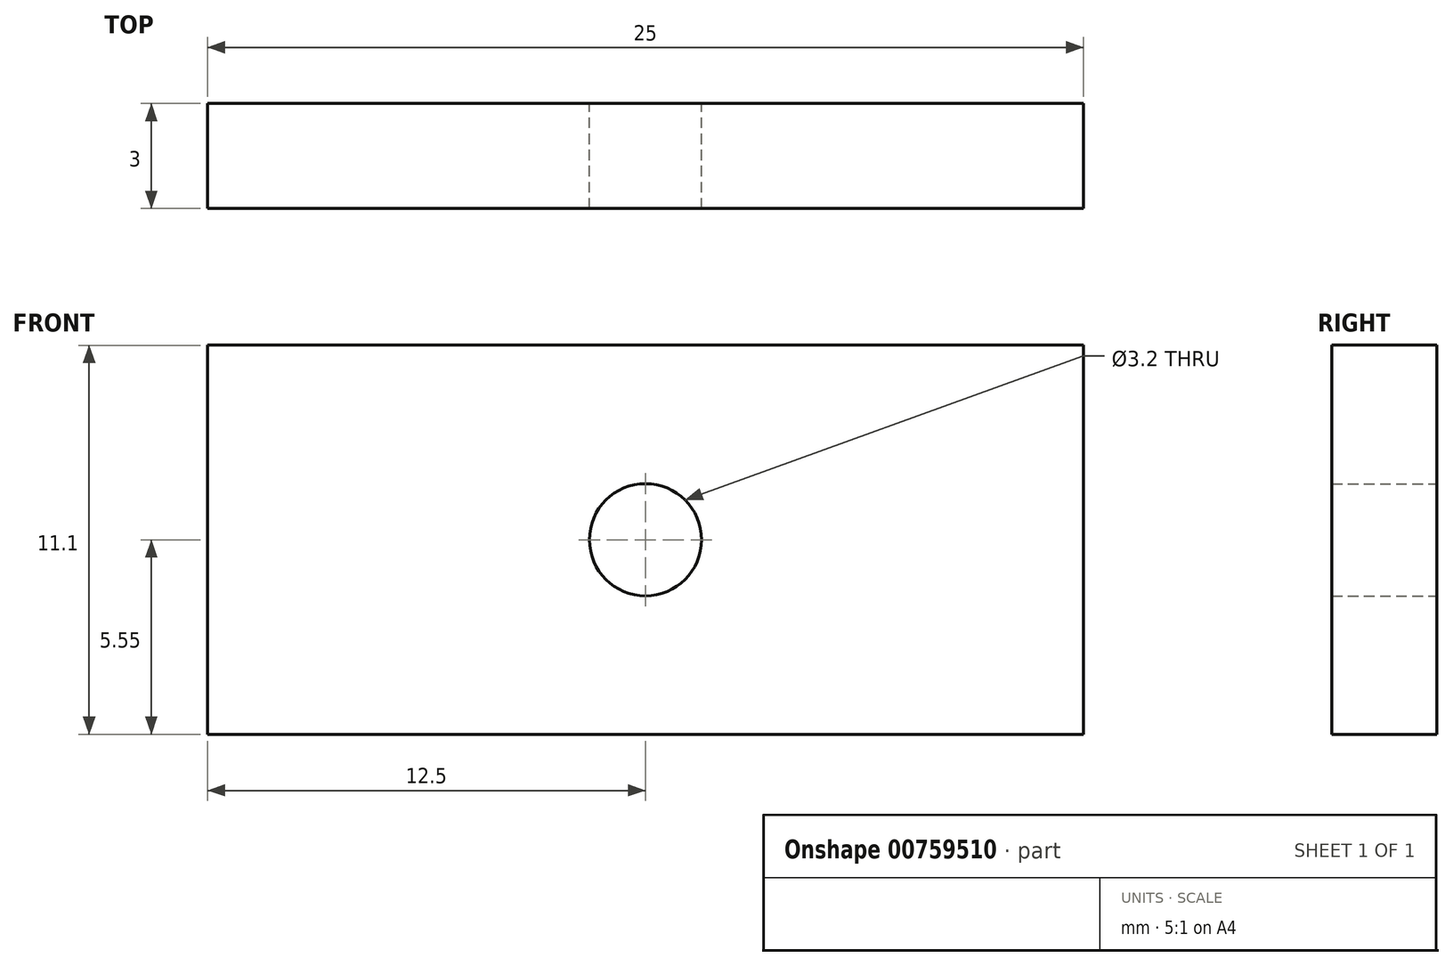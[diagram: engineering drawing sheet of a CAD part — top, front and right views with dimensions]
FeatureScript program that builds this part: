
annotation { "Feature Type Name" : "Feature", "Feature Type Description" : "" }
export const myFeature = defineFeature(function(context is Context, id is Id, definition is map)
    precondition{}
    {
        {
            var Q0;
            Q0=qCreatedBy(makeId("Front.planeOp"),FACE);
            var sketch = newSketch(context, id + "F0", { "sketchPlane" : qUnion([Q0])});
            skLineSegment(sketch, "E0.bottom", {"start": v(-12.5, 5.55) * mm, "end": v(12.5, 5.55) * mm});
            skLineSegment(sketch, "E0.top", {"start": v(-12.5, -5.56) * mm, "end": v(12.5, -5.56) * mm});
            skLineSegment(sketch, "E0.left", {"start": v(-12.5, 5.55) * mm, "end": v(-12.5, -5.56) * mm});
            skLineSegment(sketch, "E0.right", {"start": v(12.5, 5.56) * mm, "end": v(12.5, -5.56) * mm});
            skPoint(sketch, "E0.middle", {"position": v(0, 0) * mm});
            skCircle(sketch, "E1", {"center": v(0, 0) * mm, "radius": 1.6 * mm});
            skSolve(sketch);
        }
        {
            var Q0;
            Q0 = qSketchRegion(id + "F0", true);
            extrude(context, id + "F1", {"entities" : qUnion([Q0]), "depth" : 3 * mm, "offsetDistance" : 25 * mm});
        }
    });
